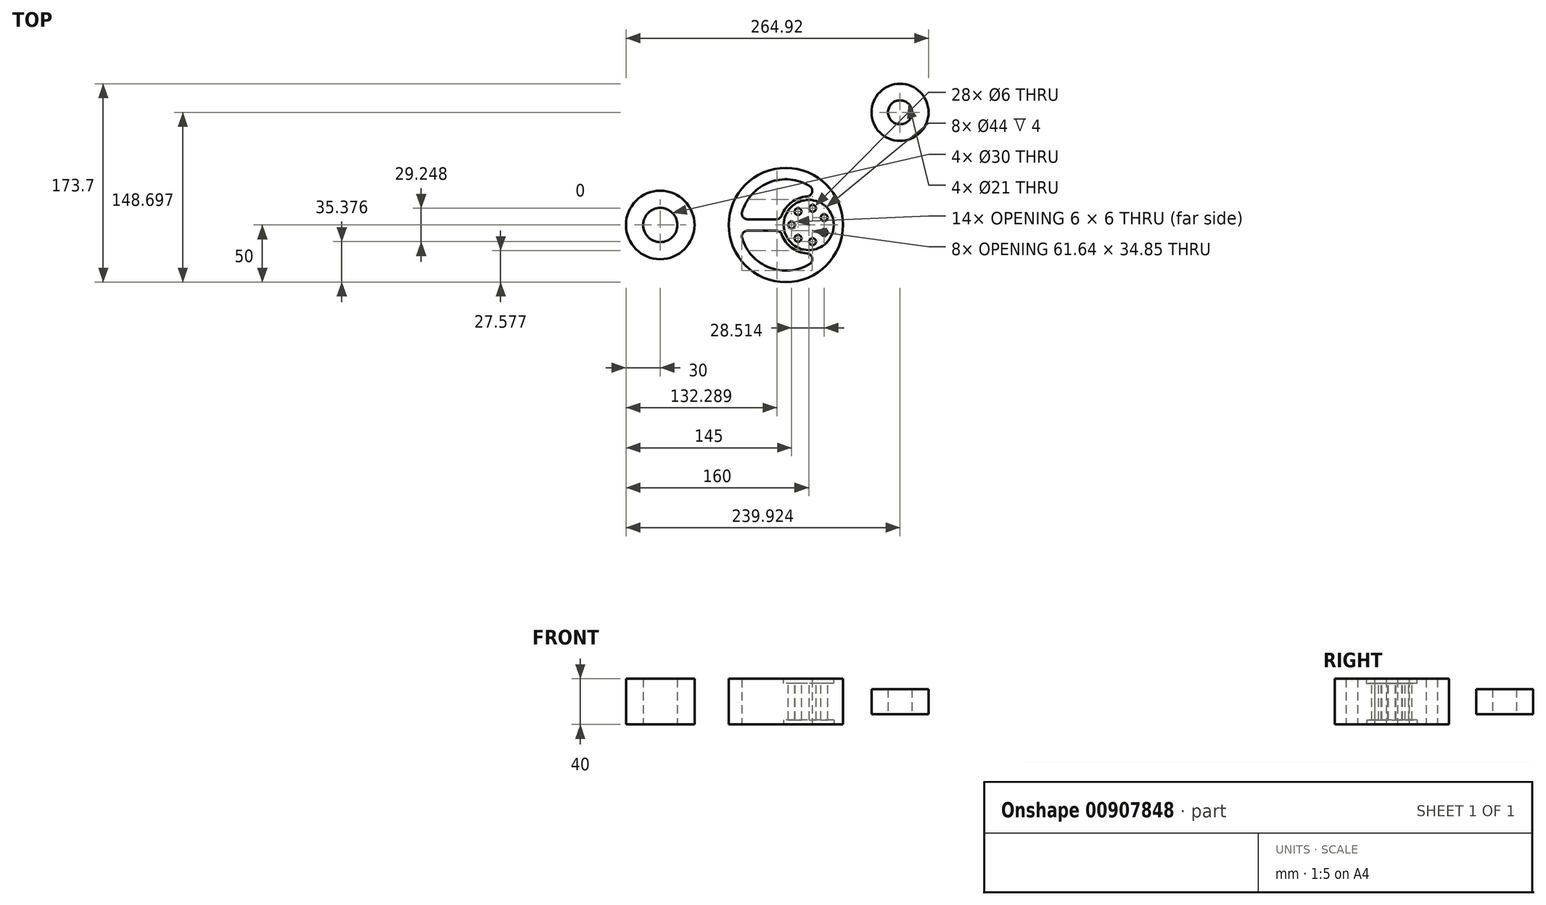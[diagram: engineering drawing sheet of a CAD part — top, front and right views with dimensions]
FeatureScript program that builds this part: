
annotation { "Feature Type Name" : "Feature", "Feature Type Description" : "" }
export const myFeature = defineFeature(function(context is Context, id is Id, definition is map)
    precondition{}
    {
        {
            var Q0;
            Q0=qCreatedBy(makeId("Top.planeOp"),FACE);
            var sketch = newSketch(context, id + "F0", { "sketchPlane" : qUnion([Q0])});
            skCircle(sketch, "E0", {"center": v(-20, 0) * mm, "radius": 50 * mm});
            skSolve(sketch);
        }
        {
            var Q0;
            Q0=qCreatedBy(makeId("Top.planeOp"),FACE);
            var sketch = newSketch(context, id + "F1", { "sketchPlane" : qUnion([Q0])});
            skArc(sketch, "E1", {"start": v(-59.69, -5) * mm, "mid": v(-28.17, -39.16) * mm, "end": v(14.38, -20.45) * mm});
            skLineSegment(sketch, "E2", {"start": v(-59.69, 5) * mm, "end": v(-24.5, 5) * mm});
            skLineSegment(sketch, "E3", {"start": v(-59.69, -5) * mm, "end": v(-24.5, -5) * mm});
            skArc(sketch, "E4", {"start": v(14.37, 20.45) * mm, "mid": v(-9.24, 23.23) * mm, "end": v(-24.5, 5) * mm});
            skArc(sketch, "E5.trimOffspring", {"start": v(14.37, 20.45) * mm, "mid": v(-28.17, 39.16) * mm, "end": v(-59.69, 5) * mm});
            skArc(sketch, "E6.trimOffspring", {"start": v(-24.5, -5) * mm, "mid": v(-9.24, -23.23) * mm, "end": v(14.37, -20.45) * mm});
            skSolve(sketch);
        }
        {
            var Q0;
            Q0=makeQuery(id+"F0.imprint","IMPRINT",FACE,{"disambiguationData":[TD([[makeQuery(id+"F0.imprint","IMPRINT",EDGE,{"derivedFrom":sQuery(id+"F0.wireOp",EDGE,"E0")}),1.0]])]});
            extrude(context, id + "F2", {"entities" : qUnion([Q0]), "endBound" : BoundingType.SYMMETRIC, "depth" : 40 * mm, "offsetDistance" : 25 * mm});
        }
        {
            var Q0;
            Q0 = qSketchRegion(id + "F1", true);
            extrude(context, id + "F3", {"entities" : qUnion([Q0]), "endBound" : BoundingType.SYMMETRIC, "depth" : 89 * mm, "offsetDistance" : 25 * mm});
        }
        {
            var Q0;
            Q0=makeQuery(id+"F3.opExtrude","SWEPT_BODY",BODY,{"disambiguationData":[OSD([sQuery(id+"F1.wireOp",EDGE,"E2"),sQuery(id+"F1.wireOp",EDGE,"E4"),sQuery(id+"F1.wireOp",EDGE,"E5.trimOffspring")])]});
            var Q1;
            Q1=makeQuery(id+"F3.opExtrude","SWEPT_BODY",BODY,{"disambiguationData":[OSD([sQuery(id+"F1.wireOp",EDGE,"E1"),sQuery(id+"F1.wireOp",EDGE,"E3"),sQuery(id+"F1.wireOp",EDGE,"E6.trimOffspring")])]});
            var Q2;
            Q2=makeQuery(id+"F2.opExtrude","SWEPT_BODY",BODY,{"disambiguationData":[OSD([sQuery(id+"F0.wireOp",EDGE,"E0")])]});
            booleanBodies(context, id + "F4", {"operationType" : BooleanOperationType.SUBTRACTION, "tools" : qUnion([Q0, Q1]), "targets" : qUnion([Q2])});
        }
        {
            var Q0;
            Q0=makeQuery(id+"F4.opBoolean","COPY",EDGE,{"derivedFrom":makeQuery(id+"F3.opExtrude","SWEPT_EDGE",EDGE,{"disambiguationData":[OSD([sQuery(id+"F1.wireOp",EDGE,"E4"),sQuery(id+"F1.wireOp",EDGE,"E5.trimOffspring")])]})});
            var Q1;
            Q1=makeQuery(id+"F4.opBoolean","COPY",EDGE,{"derivedFrom":makeQuery(id+"F3.opExtrude","SWEPT_EDGE",EDGE,{"disambiguationData":[OSD([sQuery(id+"F1.wireOp",EDGE,"E2"),sQuery(id+"F1.wireOp",EDGE,"E5.trimOffspring")])]})});
            var Q2;
            Q2=makeQuery(id+"F4.opBoolean","COPY",EDGE,{"derivedFrom":makeQuery(id+"F3.opExtrude","SWEPT_EDGE",EDGE,{"disambiguationData":[OSD([sQuery(id+"F1.wireOp",EDGE,"E2"),sQuery(id+"F1.wireOp",EDGE,"E4")])]})});
            var Q3;
            Q3=makeQuery(id+"F4.opBoolean","COPY",EDGE,{"derivedFrom":makeQuery(id+"F3.opExtrude","SWEPT_EDGE",EDGE,{"disambiguationData":[OSD([sQuery(id+"F1.wireOp",EDGE,"E3"),sQuery(id+"F1.wireOp",EDGE,"E6.trimOffspring")])]})});
            var Q4;
            Q4=makeQuery(id+"F4.opBoolean","COPY",EDGE,{"derivedFrom":makeQuery(id+"F3.opExtrude","SWEPT_EDGE",EDGE,{"disambiguationData":[OSD([sQuery(id+"F1.wireOp",EDGE,"E1"),sQuery(id+"F1.wireOp",EDGE,"E3")])]})});
            var Q5;
            Q5=makeQuery(id+"F4.opBoolean","COPY",EDGE,{"derivedFrom":makeQuery(id+"F3.opExtrude","SWEPT_EDGE",EDGE,{"disambiguationData":[OSD([sQuery(id+"F1.wireOp",EDGE,"E1"),sQuery(id+"F1.wireOp",EDGE,"E6.trimOffspring")])]})});
            fillet(context, id + "F5", {"entities" : qUnion([Q0, Q1, Q2, Q3, Q4, Q5]), "radius" : 5 * mm, "tangentPropagation" : true, "allowEdgeOverflow" : false});
        }
        {
            var Q0;
            Q0=makeQuery(id+"F2.opExtrude","CAP_FACE",FACE,{"disambiguationData":[OSD([sQuery(id+"F0.wireOp",EDGE,"E0")])],"isStart":false});
            var sketch = newSketch(context, id + "F6", { "sketchPlane" : qUnion([Q0])});
            skCircle(sketch, "E7", {"center": v(0, 0) * mm, "radius": 22 * mm});
            skSolve(sketch);
        }
        {
            var Q0;
            Q0 = qSketchRegion(id + "F6", true);
            extrude(context, id + "F7", {"entities" : qUnion([Q0]), "oppositeDirection" : true, "depth" : 4 * mm, "offsetDistance" : 25 * mm, "hasSecondDirection" : true, "secondDirectionOppositeDirection" : true, "secondDirectionDepth" : -10 * mm});
        }
        {
            var Q0;
            Q0=makeQuery(id+"F7.opExtrude","SWEPT_BODY",BODY,{"disambiguationData":[OSD([sQuery(id+"F6.wireOp",EDGE,"E7")])]});
            var Q1;
            Q1=qCreatedBy(makeId("Top.planeOp"),FACE);
            mirror(context, id + "F8", {"entities" : qUnion([Q0]), "mirrorPlane" : qUnion([Q1])});
        }
        {
            var Q0;
            Q0=makeQuery(id+"F7.opExtrude","SWEPT_BODY",BODY,{"disambiguationData":[OSD([sQuery(id+"F6.wireOp",EDGE,"E7")])]});
            var Q1;
            Q1=makeQuery(id+"F8.opPattern","COPY",BODY,{"derivedFrom":makeQuery(id+"F7.opExtrude","SWEPT_BODY",BODY,{"disambiguationData":[OSD([sQuery(id+"F6.wireOp",EDGE,"E7")])]}),"instanceName":"1"});
            var Q2;
            Q2=makeQuery(id+"F2.opExtrude","SWEPT_BODY",BODY,{"disambiguationData":[OSD([sQuery(id+"F0.wireOp",EDGE,"E0")])]});
            booleanBodies(context, id + "F9", {"operationType" : BooleanOperationType.SUBTRACTION, "tools" : qUnion([Q0, Q1]), "targets" : qUnion([Q2])});
        }
        {
            var Q0;
            Q0=makeQuery(id+"F2.opExtrude","CAP_FACE",FACE,{"disambiguationData":[OSD([sQuery(id+"F0.wireOp",EDGE,"E0")])],"isStart":false});
            var sketch = newSketch(context, id + "F10", { "sketchPlane" : qUnion([Q0])});
            skPoint(sketch, "E8", {"position": v(-15, 0) * mm});
            skCircle(sketch, "E9", {"center": v(-15, 0) * mm, "radius": 3 * mm});
            skSolve(sketch);
        }
        {
            var Q0;
            Q0=makeQuery(id+"F10.imprint","IMPRINT",FACE,{"disambiguationData":[TD([[makeQuery(id+"F10.imprint","IMPRINT",EDGE,{"derivedFrom":sQuery(id+"F10.wireOp",EDGE,"E9")}),1.0]])]});
            extrude(context, id + "F11", {"entities" : qUnion([Q0]), "oppositeDirection" : true, "depth" : 60 * mm, "offsetDistance" : 25 * mm});
        }
        {
            var Q0;
            Q0=makeQuery(id+"F11.opExtrude","SWEPT_BODY",BODY,{"disambiguationData":[OSD([sQuery(id+"F10.wireOp",EDGE,"E9")])]});
            var Q1;
            Q1=makeQuery(id+"F9.opBoolean","INTERSECT",EDGE,{"derivedFrom":[makeQuery(id+"F2.opExtrude","CAP_FACE",FACE,{"disambiguationData":[OSD([sQuery(id+"F0.wireOp",EDGE,"E0")])],"isStart":false}),makeQuery(id+"F7.opExtrude","SWEPT_FACE",FACE,{"disambiguationData":[OSD([sQuery(id+"F6.wireOp",EDGE,"E7")])]})]});
            circularPattern(context, id + "F12", {"entities" : qUnion([Q0]), "axis" : qUnion([Q1]), "angle" : 360 * degree, "instanceCount" : 7, "equalSpace" : true});
        }
        {
            var Q0;
            Q0=makeQuery(id+"F12.opPattern","COPY",BODY,{"derivedFrom":makeQuery(id+"F11.opExtrude","SWEPT_BODY",BODY,{"disambiguationData":[OSD([sQuery(id+"F10.wireOp",EDGE,"E9")])]}),"instanceName":"5"});
            var Q1;
            Q1=makeQuery(id+"F12.opPattern","COPY",BODY,{"derivedFrom":makeQuery(id+"F11.opExtrude","SWEPT_BODY",BODY,{"disambiguationData":[OSD([sQuery(id+"F10.wireOp",EDGE,"E9")])]}),"instanceName":"3"});
            var Q2;
            Q2=makeQuery(id+"F12.opPattern","COPY",BODY,{"derivedFrom":makeQuery(id+"F11.opExtrude","SWEPT_BODY",BODY,{"disambiguationData":[OSD([sQuery(id+"F10.wireOp",EDGE,"E9")])]}),"instanceName":"4"});
            var Q3;
            Q3=makeQuery(id+"F11.opExtrude","SWEPT_BODY",BODY,{"disambiguationData":[OSD([sQuery(id+"F10.wireOp",EDGE,"E9")])]});
            var Q4;
            Q4=makeQuery(id+"F12.opPattern","COPY",BODY,{"derivedFrom":makeQuery(id+"F11.opExtrude","SWEPT_BODY",BODY,{"disambiguationData":[OSD([sQuery(id+"F10.wireOp",EDGE,"E9")])]}),"instanceName":"6"});
            var Q5;
            Q5=makeQuery(id+"F12.opPattern","COPY",BODY,{"derivedFrom":makeQuery(id+"F11.opExtrude","SWEPT_BODY",BODY,{"disambiguationData":[OSD([sQuery(id+"F10.wireOp",EDGE,"E9")])]}),"instanceName":"1"});
            var Q6;
            Q6=makeQuery(id+"F12.opPattern","COPY",BODY,{"derivedFrom":makeQuery(id+"F11.opExtrude","SWEPT_BODY",BODY,{"disambiguationData":[OSD([sQuery(id+"F10.wireOp",EDGE,"E9")])]}),"instanceName":"2"});
            var Q7;
            Q7=makeQuery(id+"F2.opExtrude","SWEPT_BODY",BODY,{"disambiguationData":[OSD([sQuery(id+"F0.wireOp",EDGE,"E0")])]});
            booleanBodies(context, id + "F13", {"operationType" : BooleanOperationType.SUBTRACTION, "tools" : qUnion([Q0, Q1, Q2, Q3, Q4, Q5, Q6]), "targets" : qUnion([Q7])});
        }
        {
            var Q0;
            Q0=qCreatedBy(makeId("Top.planeOp"),FACE);
            var sketch = newSketch(context, id + "F14", { "sketchPlane" : qUnion([Q0])});
            skCircle(sketch, "E10", {"center": v(79.92, 98.7) * mm, "radius": 25 * mm});
            skCircle(sketch, "E11", {"center": v(79.92, 98.7) * mm, "radius": 10.5 * mm});
            skLineSegment(sketch, "E12", {"start": v(0, 0) * mm, "end": v(79.92, 98.7) * mm, "construction": true});
            skLineSegment(sketch, "E13", {"start": v(0, 0) * mm, "end": v(125, 0) * mm, "construction": true});
            skCircle(sketch, "E14", {"center": v(-130, 0) * mm, "radius": 30 * mm});
            skCircle(sketch, "E15", {"center": v(-130, 0) * mm, "radius": 15 * mm});
            skSolve(sketch);
        }
        {
            var Q0;
            Q0=makeQuery(id+"F14.imprint","IMPRINT",FACE,{"disambiguationData":[TD([[makeQuery(id+"F14.imprint","IMPRINT",EDGE,{"derivedFrom":sQuery(id+"F14.wireOp",EDGE,"E14")}),1.0]])]});
            extrude(context, id + "F15", {"entities" : qUnion([Q0]), "endBound" : BoundingType.SYMMETRIC, "depth" : 40 * mm, "offsetDistance" : 25 * mm});
        }
        {
            var Q0;
            Q0=makeQuery(id+"F14.imprint","IMPRINT",FACE,{"disambiguationData":[TD([[makeQuery(id+"F14.imprint","IMPRINT",EDGE,{"derivedFrom":sQuery(id+"F14.wireOp",EDGE,"E10")}),1.0]])]});
            extrude(context, id + "F16", {"entities" : qUnion([Q0]), "endBound" : BoundingType.SYMMETRIC, "depth" : 22 * mm, "offsetDistance" : 25 * mm});
        }
    });
